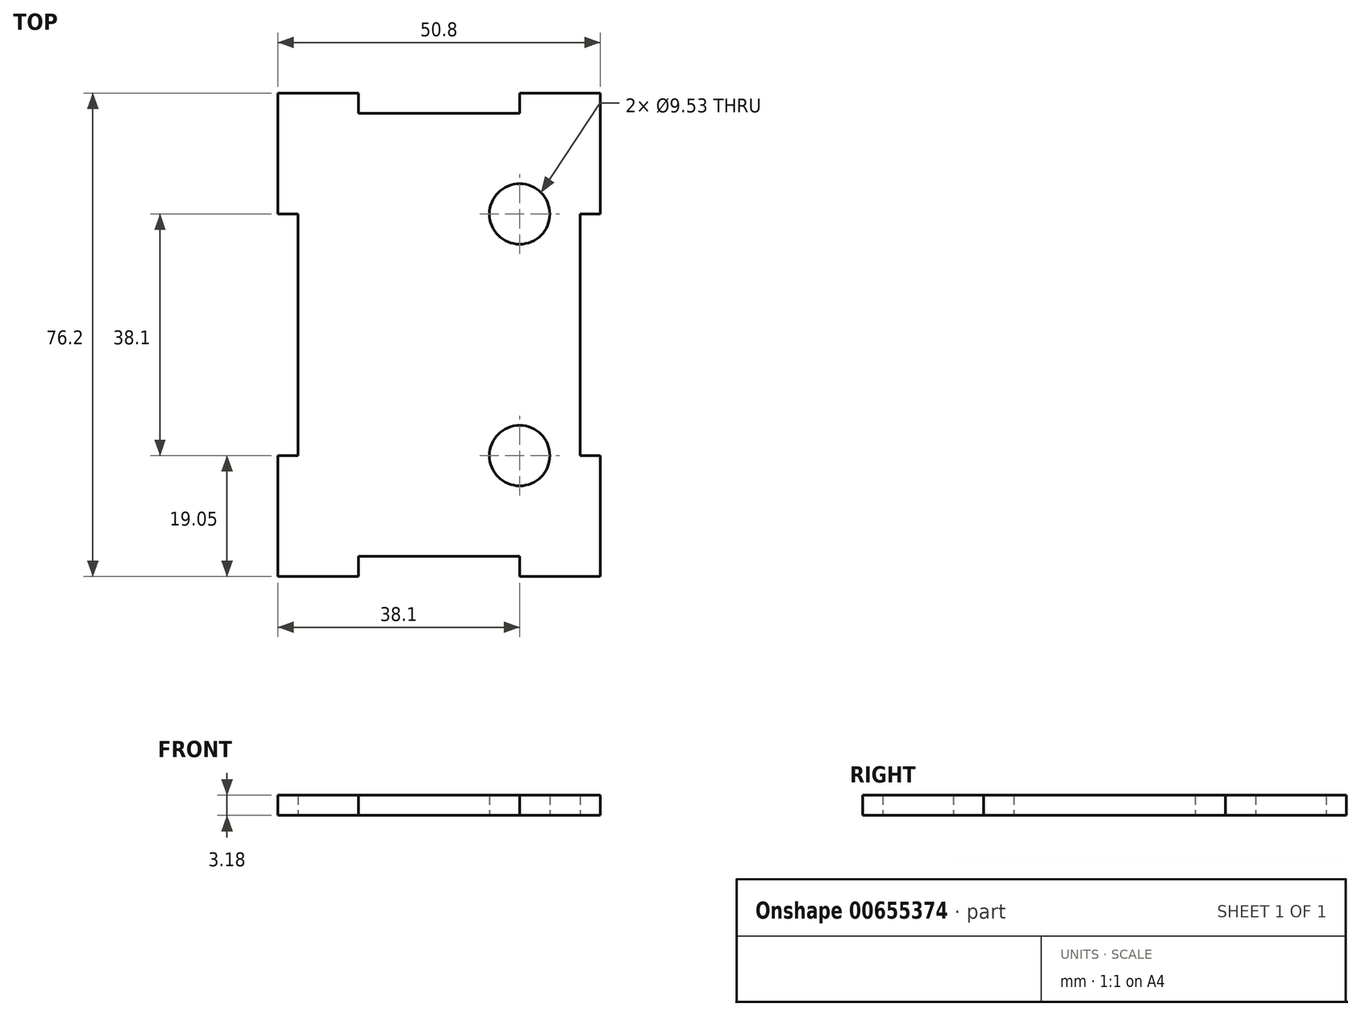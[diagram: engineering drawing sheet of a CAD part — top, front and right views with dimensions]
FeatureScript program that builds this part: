
annotation { "Feature Type Name" : "Feature", "Feature Type Description" : "" }
export const myFeature = defineFeature(function(context is Context, id is Id, definition is map)
    precondition{}
    {
        {
            var Q0;
            Q0=qCreatedBy(makeId("Top.planeOp"),FACE);
            var sketch = newSketch(context, id + "F0", { "sketchPlane" : qUnion([Q0])});
            skLineSegment(sketch, "E0.bottom", {"start": v(25.4, 38.1) * mm, "end": v(12.7, 38.1) * mm});
            skLineSegment(sketch, "E0.top", {"start": v(25.4, -38.1) * mm, "end": v(12.7, -38.1) * mm});
            skLineSegment(sketch, "E0.left", {"start": v(25.4, 38.1) * mm, "end": v(25.4, 19.05) * mm});
            skLineSegment(sketch, "E0.right", {"start": v(-25.4, 38.1) * mm, "end": v(-25.4, 19.05) * mm});
            skPoint(sketch, "E0.middle", {"position": v(0, 0) * mm});
            skLineSegment(sketch, "E1.bottom", {"start": v(28.58, 19.05) * mm, "end": v(22.22, 19.05) * mm, "construction": true});
            skLineSegment(sketch, "E1.top", {"start": v(25.4, -19.05) * mm, "end": v(22.22, -19.05) * mm});
            skLineSegment(sketch, "E1.left", {"start": v(28.58, 19.05) * mm, "end": v(28.58, -19.05) * mm, "construction": true});
            skLineSegment(sketch, "E1.right", {"start": v(22.22, 19.05) * mm, "end": v(22.22, -19.05) * mm});
            skPoint(sketch, "E1.middle", {"position": v(25.4, 0) * mm});
            skLineSegment(sketch, "E2.bottom", {"start": v(12.7, 41.28) * mm, "end": v(-12.7, 41.28) * mm, "construction": true});
            skLineSegment(sketch, "E2.top", {"start": v(12.7, 34.93) * mm, "end": v(-12.7, 34.93) * mm});
            skLineSegment(sketch, "E2.left", {"start": v(12.7, 41.28) * mm, "end": v(12.7, 38.1) * mm, "construction": true});
            skLineSegment(sketch, "E2.right", {"start": v(-12.7, 41.28) * mm, "end": v(-12.7, 38.1) * mm, "construction": true});
            skPoint(sketch, "E2.middle", {"position": v(0, 38.1) * mm});
            skCircle(sketch, "E3", {"center": v(12.7, 19.05) * mm, "radius": 4.76 * mm});
            skCircle(sketch, "E4.MirrorC", {"center": v(12.7, -19.05) * mm, "radius": 4.76 * mm});
            skLineSegment(sketch, "E5.MirrorCS", {"start": v(-22.22, 19.05) * mm, "end": v(-22.22, -19.05) * mm});
            skLineSegment(sketch, "E6.MirrorCS", {"start": v(-25.4, 19.05) * mm, "end": v(-22.22, 19.05) * mm});
            skLineSegment(sketch, "E7.MirrorCS", {"start": v(-25.4, -19.05) * mm, "end": v(-22.22, -19.05) * mm});
            skLineSegment(sketch, "E8.MirrorCS", {"start": v(12.7, -34.93) * mm, "end": v(-12.7, -34.93) * mm});
            skLineSegment(sketch, "E9.MirrorCS", {"start": v(12.7, -41.28) * mm, "end": v(-12.7, -41.28) * mm, "construction": true});
            skLineSegment(sketch, "E10.MirrorCS", {"start": v(12.7, -41.28) * mm, "end": v(12.7, -34.93) * mm, "construction": true});
            skLineSegment(sketch, "E11.MirrorCS", {"start": v(-12.7, -41.28) * mm, "end": v(-12.7, -34.93) * mm, "construction": true});
            skPoint(sketch, "E12.orphan", {"position": v(-28.58, 19.05) * mm});
            skLineSegment(sketch, "E13.trimOffspring", {"start": v(-25.4, -19.05) * mm, "end": v(-25.4, -38.1) * mm});
            skPoint(sketch, "E14.MirrorCS.end.orphan", {"position": v(-28.58, -19.05) * mm});
            skLineSegment(sketch, "E15", {"start": v(25.4, 19.05) * mm, "end": v(22.22, 19.05) * mm});
            skLineSegment(sketch, "E16.trimOffspring", {"start": v(25.4, -19.05) * mm, "end": v(25.4, -38.1) * mm});
            skLineSegment(sketch, "E17", {"start": v(-12.7, -38.1) * mm, "end": v(-12.7, -34.93) * mm});
            skLineSegment(sketch, "E18", {"start": v(12.7, -38.1) * mm, "end": v(12.7, -34.93) * mm});
            skLineSegment(sketch, "E19.trimOffspring", {"start": v(-12.7, -38.1) * mm, "end": v(-25.4, -38.1) * mm});
            skLineSegment(sketch, "E20", {"start": v(12.7, 38.1) * mm, "end": v(12.7, 34.93) * mm});
            skLineSegment(sketch, "E21", {"start": v(-12.7, 38.1) * mm, "end": v(-12.7, 34.93) * mm});
            skLineSegment(sketch, "E22", {"start": v(-12.7, 38.1) * mm, "end": v(-12.7, 34.93) * mm, "construction": true});
            skLineSegment(sketch, "E23", {"start": v(12.7, 38.1) * mm, "end": v(12.7, 34.93) * mm, "construction": true});
            skLineSegment(sketch, "E24", {"start": v(-25.4, 38.1) * mm, "end": v(-12.7, 38.1) * mm});
            skLineSegment(sketch, "E25", {"start": v(12.7, 38.1) * mm, "end": v(25.4, 38.1) * mm});
            skLineSegment(sketch, "E26.trimOffspring", {"start": v(0, 38.1) * mm, "end": v(-25.4, 38.1) * mm, "construction": true});
            skLineSegment(sketch, "E27", {"start": v(-12.7, 38.1) * mm, "end": v(-25.4, 38.1) * mm, "construction": true});
            skSolve(sketch);
        }
        {
            var Q0;
            Q0=makeQuery(id+"F0.imprint","IMPRINT",FACE,{"disambiguationData":[TD([[makeQuery(id+"F0.imprint","IMPRINT",EDGE,{"derivedFrom":sQuery(id+"F0.wireOp",EDGE,"E0.top")}),-1.0]])]});
            extrude(context, id + "F1", {"entities" : qUnion([Q0]), "depth" : 3.17 * mm, "offsetDistance" : 25.4 * mm});
        }
    });
